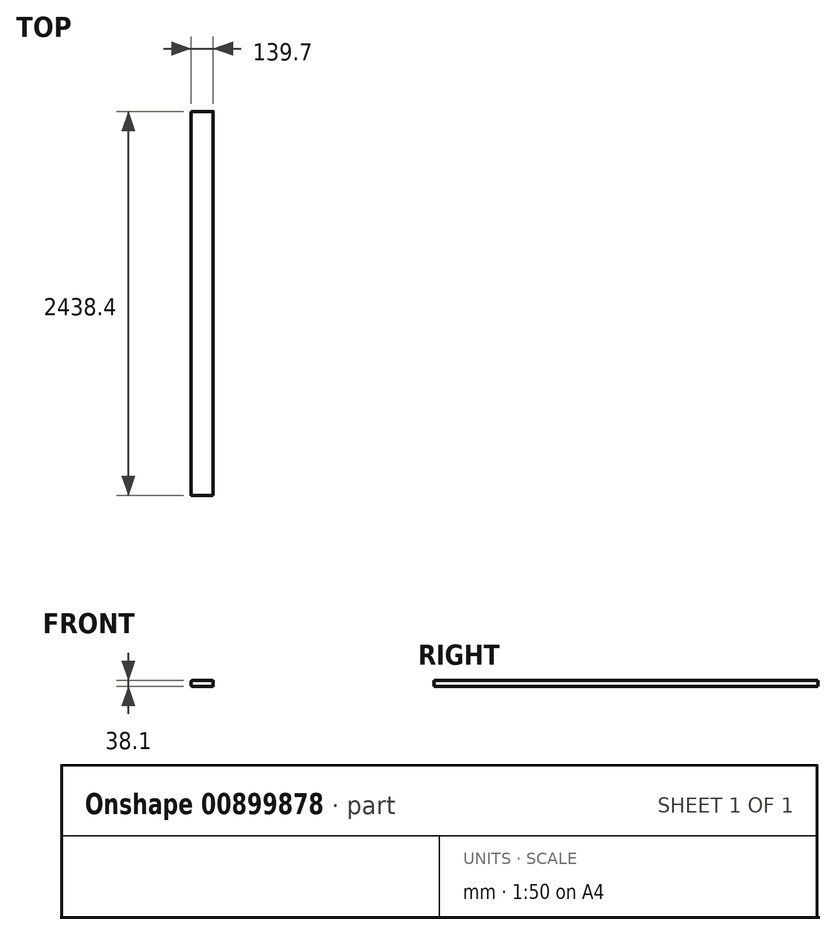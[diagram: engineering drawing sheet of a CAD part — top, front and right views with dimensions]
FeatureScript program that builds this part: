
annotation { "Feature Type Name" : "Feature", "Feature Type Description" : "" }
export const myFeature = defineFeature(function(context is Context, id is Id, definition is map)
    precondition{}
    {
        {
            var Q0;
            Q0=qCreatedBy(makeId("Front.planeOp"),FACE);
            var sketch = newSketch(context, id + "F0", { "sketchPlane" : qUnion([Q0])});
            skLineSegment(sketch, "E0.bottom", {"start": v(0, 0) * mm, "end": v(139.7, 0) * mm});
            skLineSegment(sketch, "E0.top", {"start": v(0, 38.1) * mm, "end": v(139.7, 38.1) * mm});
            skLineSegment(sketch, "E0.left", {"start": v(0, 0) * mm, "end": v(0, 38.1) * mm});
            skLineSegment(sketch, "E0.right", {"start": v(139.7, 0) * mm, "end": v(139.7, 38.1) * mm});
            skSolve(sketch);
        }
        {
            var Q0;
            Q0 = qSketchRegion(id + "F0", true);
            extrude(context, id + "F1", {"entities" : qUnion([Q0]), "depth" : 2438.4 * mm, "offsetDistance" : 25.4 * mm});
        }
        {
            var Q0;
            Q0=makeQuery(id+"F1.opExtrude","SWEPT_EDGE",EDGE,{"disambiguationData":[OSD([sQuery(id+"F0.wireOp",EDGE,"E0.top"),sQuery(id+"F0.wireOp",EDGE,"E0.right")])]});
            var Q1;
            Q1=makeQuery(id+"F1.opExtrude","SWEPT_EDGE",EDGE,{"disambiguationData":[OSD([sQuery(id+"F0.wireOp",EDGE,"E0.bottom"),sQuery(id+"F0.wireOp",EDGE,"E0.right")])]});
            var Q2;
            Q2=makeQuery(id+"F1.opExtrude","SWEPT_EDGE",EDGE,{"disambiguationData":[OSD([sQuery(id+"F0.wireOp",EDGE,"E0.top"),sQuery(id+"F0.wireOp",EDGE,"E0.left")])]});
            var Q3;
            Q3=makeQuery(id+"F1.opExtrude","SWEPT_EDGE",EDGE,{"disambiguationData":[OSD([sQuery(id+"F0.wireOp",EDGE,"E0.bottom"),sQuery(id+"F0.wireOp",EDGE,"E0.left")])]});
            fillet(context, id + "F2", {"entities" : qUnion([Q0, Q1, Q2, Q3]), "radius" : 5.08 * mm, "tangentPropagation" : true, "allowEdgeOverflow" : false});
        }
    });
